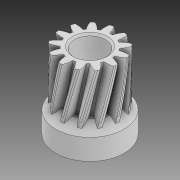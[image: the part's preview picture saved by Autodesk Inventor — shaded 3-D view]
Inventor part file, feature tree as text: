
AUTODESK INVENTOR PART (.ipt)
format: ipt  version: 2020 (Build 240168000, 168)  size: 613,376 bytes
history: native  units: mm
features: sketch x3, other x2, extrude x2, chamfer x2, revolve x1
ambient origin geometry x8: Origin, YZ Plane, XZ Plane, XY Plane, X Axis, Y Axis, Z Axis, Center Point
bodies: Solid1 (feature_tree)
feature tree (10):
  revolve  "Revolution1"  [1 undecoded]
  other  "Spur Gear Teeth1"
  extrude  "Extrusion1"  Depth=13.0mm
  extrude  "Extrusion2"  Depth=12.0mm
  chamfer  "Chamfer1"  Distance=3.55mm
  chamfer  "Chamfer2"  Distance=6.0mm
  sketch  "Sketch1"  dims[d0=4.1mm d2=8.0mm]
  other  "Spur Gear2"
  sketch  "Sketch2"  dims[d3=9.0mm d4=13.0mm]
  sketch  "Sketch3"  dims[d5=90.0deg d6=12.0mm d7=3.55mm d8=2.3mm d9=5.7mm d10=6.0mm d11=0.0mm d12=2.85mm d13=3.2mm d14=6.0mm d15=0.0mm d16=2.5mm d17=2.0mm d18=45.0deg d19=0.5mm d20=2.0mm d21=45.0deg]
note: 1 required parameter value undecoded (feature->parameter linkage not recoverable at this tier; creation-order binding heuristic only, values carry confidence <= 0.55)
